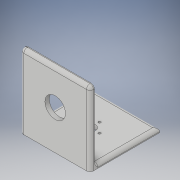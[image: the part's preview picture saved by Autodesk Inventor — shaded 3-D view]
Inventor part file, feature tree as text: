
AUTODESK INVENTOR PART (.ipt)
format: ipt  version: 2017 (Build 210142000, 142)  size: 220,160 bytes
history: native  units: in
note: dims shown in document units (in); Inventor stores cm internally (conversion verified against a paired STEP export)
features: extrude x6, sketch x6, hole x4, fillet x2, projected_geometry x1
ambient origin geometry x8: Origin, YZ Plane, XZ Plane, XY Plane, X Axis, Y Axis, Z Axis, Center Point
bodies: Solid1 (feature_tree)
feature tree (19):
  extrude  "Extrusion1"  Depth=2.0in
  extrude  "Extrusion2"  Depth=0.125in
  extrude  "Extrusion3"  Depth=0.125in
  extrude  "Extrusion4"  Depth=0.59in
  extrude  "Extrusion5"  Depth=0.25in
  fillet  "Fillet1"  Radius=0.15in
  hole  "Hole1"  [1 undecoded]
  hole  "Hole2"  [1 undecoded]
  hole  "Hole3"  [1 undecoded]
  hole  "Hole4"  [1 undecoded]
  fillet  "Fillet2"  Radius=0.075in
  extrude  "Extrusion6"  Depth=0.1in
  sketch  "Sketch1"  dims[d0=2.0in d1=2.0in]
  sketch  "Sketch2"  dims[d2=0.125in d3=0.0in d4=0.3125in]
  sketch  "Sketch3"  dims[d5=0.125in d6=0.0in d7=0.125in]
  sketch  "Sketch4"  dims[d8=2.0in d9=0.0in d10=0.59in]
  sketch  "Sketch5"  dims[d11=2.0in d12=0.0in d13=0.25in d14=0.15in]
  projected_geometry  "Projected Loop1"
  sketch  "Sketch6"  dims[d15=0.15in d16=0.15in d17=0.15in d18=0.075in d19=0.075in d20=0.075in d21=0.075in d22=0.075in d23=0.075in d24=0.075in d25=0.075in d26=0.135in d27=0.0in d28=0.0312in d29=1.0in d30=1.0in d31=0.0785in d32=0.75in d33=0.375in d34=0.25in d35=0.5635in d36=0.175in d37=0.0in d38=1.0in d39=1.0in d40=0.0785in d41=0.75in d42=0.375in d43=0.25in d44=0.5635in d45=0.175in d46=0.0in d47=1.0in d48=1.0in d49=0.0785in d50=0.75in d51=0.375in d52=0.25in d53=0.5635in d54=0.175in d55=0.0in d56=1.0in d57=1.0in d58=0.0785in d59=0.75in d60=0.375in d61=0.25in d62=0.5635in d63=0.175in d64=0.0in d65=0.1in d66=0.275in d67=0.07in d68=0.07in d69=0.275in d70=0.07in d71=0.07in d72=0.275in d73=0.275in d74=1.0in d75=0.0in]
note: 4 required parameter values undecoded (feature->parameter linkage not recoverable at this tier; creation-order binding heuristic only, values carry confidence <= 0.55)
